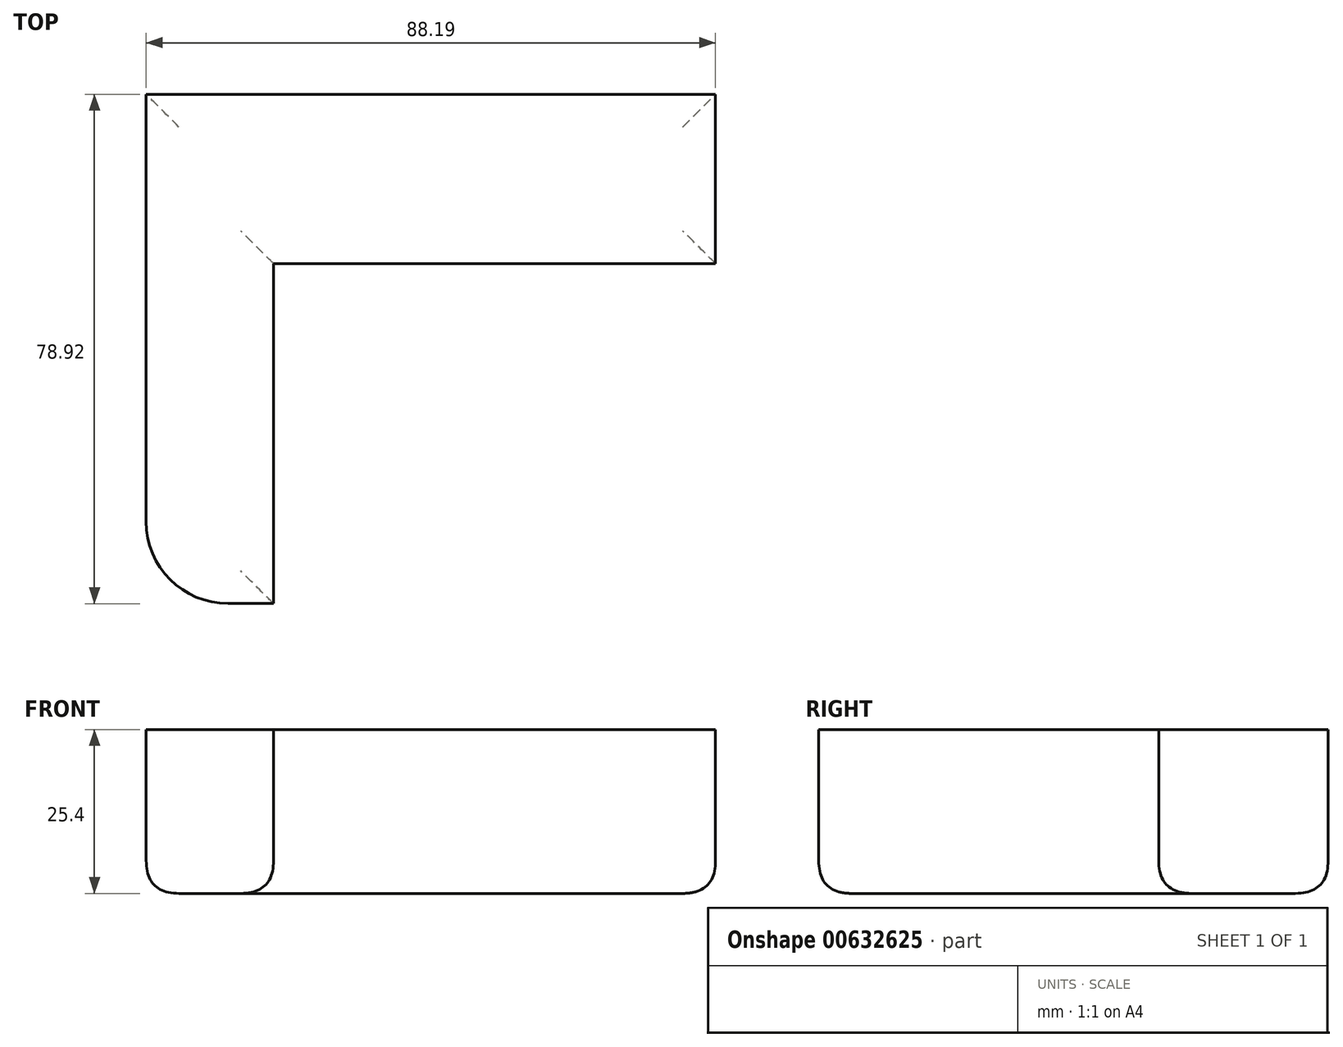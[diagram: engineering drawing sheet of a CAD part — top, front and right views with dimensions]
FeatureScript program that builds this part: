
annotation { "Feature Type Name" : "Feature", "Feature Type Description" : "" }
export const myFeature = defineFeature(function(context is Context, id is Id, definition is map)
    precondition{}
    {
        {
            var Q0;
            Q0=qCreatedBy(makeId("Top.planeOp"),FACE);
            var sketch = newSketch(context, id + "F0", { "sketchPlane" : qUnion([Q0])});
            skLineSegment(sketch, "E0.bottom", {"start": v(-36.93, 42.89) * mm, "end": v(-17.21, 42.89) * mm});
            skLineSegment(sketch, "E0.top", {"start": v(-24.23, -36.03) * mm, "end": v(-17.21, -36.03) * mm});
            skLineSegment(sketch, "E0.left", {"start": v(-36.93, 42.89) * mm, "end": v(-36.93, -23.33) * mm});
            skLineSegment(sketch, "E0.right", {"start": v(-17.21, 16.65) * mm, "end": v(-17.21, -36.03) * mm});
            skLineSegment(sketch, "E1.bottom", {"start": v(-36.93, 42.89) * mm, "end": v(51.26, 42.89) * mm});
            skLineSegment(sketch, "E1.top", {"start": v(-17.21, 16.65) * mm, "end": v(51.26, 16.65) * mm});
            skLineSegment(sketch, "E1.left", {"start": v(-36.93, 42.89) * mm, "end": v(-36.93, 16.65) * mm});
            skLineSegment(sketch, "E1.right", {"start": v(51.26, 42.89) * mm, "end": v(51.26, 16.65) * mm});
            skPoint(sketch, "E2.visualSharp", {"position": v(-36.93, -36.03) * mm});
            skArc(sketch, "E2.filletArc", {"start": v(-36.93, -23.33) * mm, "mid": v(-33.22, -32.3) * mm, "end": v(-24.23, -36.03) * mm});
            skSolve(sketch);
        }
        {
            var Q0;
            Q0 = qSketchRegion(id + "F0", true);
            extrude(context, id + "F1", {"entities" : qUnion([Q0]), "depth" : 25.4 * mm, "offsetDistance" : 25.4 * mm});
        }
        {
            var Q0;
            Q0=makeQuery(id+"F1.opExtrude","CAP_FACE",FACE,{"disambiguationData":[OSD([sQuery(id+"F0.wireOp",EDGE,"E0.top"),sQuery(id+"F0.wireOp",EDGE,"E0.left"),sQuery(id+"F0.wireOp",EDGE,"E0.right"),sQuery(id+"F0.wireOp",EDGE,"E1.bottom"),sQuery(id+"F0.wireOp",EDGE,"E1.top"),sQuery(id+"F0.wireOp",EDGE,"E1.left"),sQuery(id+"F0.wireOp",EDGE,"E1.right"),sQuery(id+"F0.wireOp",EDGE,"E2.filletArc")])],"isStart":true});
            fillet(context, id + "F2", {"entities" : qUnion([Q0]), "radius" : 5.08 * mm, "tangentPropagation" : true, "rho" : 0.5, "crossSection" : FilletCrossSection.CONIC, "allowEdgeOverflow" : false});
        }
    });
